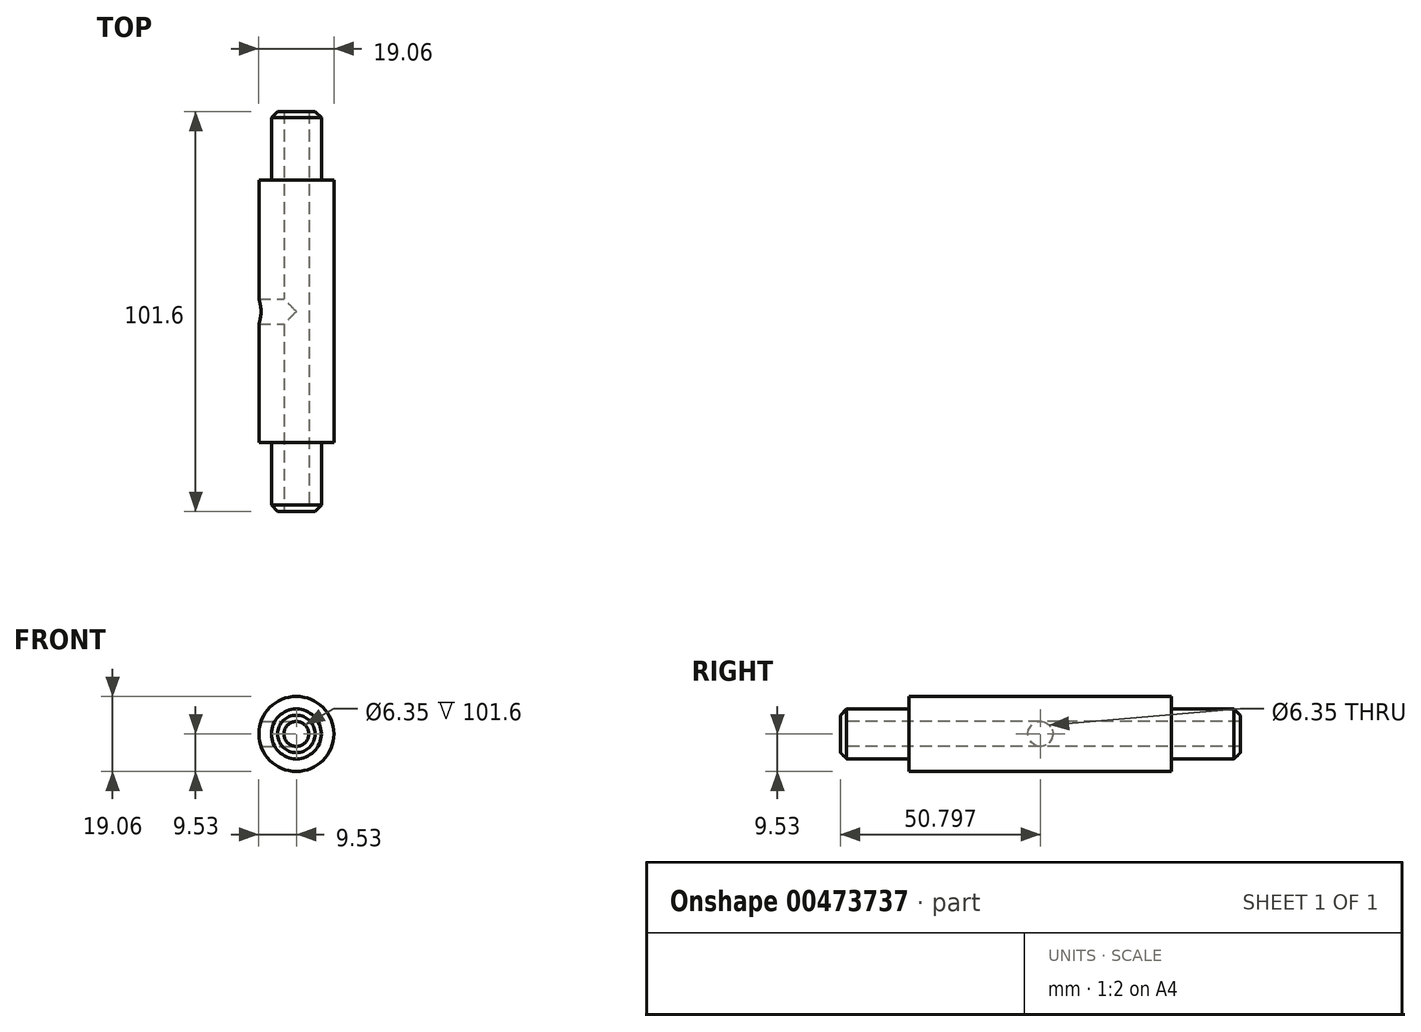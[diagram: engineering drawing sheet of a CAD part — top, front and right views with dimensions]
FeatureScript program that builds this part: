
annotation { "Feature Type Name" : "Feature", "Feature Type Description" : "" }
export const myFeature = defineFeature(function(context is Context, id is Id, definition is map)
    precondition{}
    {
        {
            var Q0;
            Q0=qCreatedBy(makeId("Right.planeOp"),FACE);
            var sketch = newSketch(context, id + "F0", { "sketchPlane" : qUnion([Q0])});
            skLineSegment(sketch, "E0", {"start": v(-10.14, 0) * mm, "end": v(91.46, 0) * mm});
            skLineSegment(sketch, "E1", {"start": v(-10.14, 3.18) * mm, "end": v(91.46, 3.18) * mm});
            skLineSegment(sketch, "E2", {"start": v(47, 3.17) * mm, "end": v(47, 0) * mm});
            skLineSegment(sketch, "E3", {"start": v(7.32, 3.17) * mm, "end": v(7.32, 9.53) * mm});
            skLineSegment(sketch, "E4", {"start": v(-10.14, 3.18) * mm, "end": v(-10.14, 6.35) * mm});
            skLineSegment(sketch, "E5", {"start": v(-10.14, 6.35) * mm, "end": v(7.32, 6.35) * mm});
            skPoint(sketch, "E5.endSnap0", {"position": v(7.32, 6.35) * mm});
            skLineSegment(sketch, "E6", {"start": v(7.32, 9.53) * mm, "end": v(74, 9.53) * mm});
            skLineSegment(sketch, "E7", {"start": v(91.46, 3.18) * mm, "end": v(91.46, 6.35) * mm});
            skLineSegment(sketch, "E8", {"start": v(74, 9.53) * mm, "end": v(74, 6.35) * mm});
            skLineSegment(sketch, "E9", {"start": v(74, 6.35) * mm, "end": v(91.46, 6.35) * mm});
            skSolve(sketch);
        }
        {
            var Q0;
            {var subQ0=sQuery(id+"F0.wireOp",EDGE,"E4");Q0=makeQuery(id+"F0.imprint","IMPRINT",FACE,{"disambiguationData":[TD([[makeQuery(id+"F0.imprint","IMPRINT",EDGE,{"derivedFrom":subQ0}),-1.0]])]});}
            var Q1;
            {var subQ0=sQuery(id+"F0.wireOp",EDGE,"E6");Q1=makeQuery(id+"F0.imprint","IMPRINT",FACE,{"disambiguationData":[TD([[makeQuery(id+"F0.imprint","IMPRINT",EDGE,{"derivedFrom":subQ0}),-1.0]])]});}
            var Q2;
            Q2=sQuery(id+"F0.wireOp",EDGE,"E0");
            revolve(context, id + "F1", {"entities" : qUnion([Q0, Q1]), "axis" : qUnion([Q2]), "revolveType" : RevolveType.FULL});
        }
        {
            var Q0;
            Q0=qCreatedBy(makeId("Right.planeOp"),FACE);
            var sketch = newSketch(context, id + "F2", { "sketchPlane" : qUnion([Q0])});
            skLineSegment(sketch, "E10.bottom", {"start": v(-30.78, -6.48) * mm, "end": v(-44.46, -6.48) * mm});
            skLineSegment(sketch, "E10.top", {"start": v(-30.78, 6.48) * mm, "end": v(-44.46, 6.48) * mm});
            skLineSegment(sketch, "E10.left", {"start": v(-30.78, -6.48) * mm, "end": v(-30.78, 6.48) * mm});
            skLineSegment(sketch, "E10.right", {"start": v(-44.46, -6.48) * mm, "end": v(-44.46, 6.48) * mm});
            skPoint(sketch, "E10.middle", {"position": v(-37.62, 0) * mm});
            skSolve(sketch);
        }
        {
            var Q0;
            Q0=makeQuery(id+"F2.imprint","IMPRINT",FACE,{"disambiguationData":[TD([[makeQuery(id+"F2.imprint","IMPRINT",EDGE,{"derivedFrom":sQuery(id+"F2.wireOp",EDGE,"E10.bottom")}),-1.0]])]});
            extrude(context, id + "F3", {"entities" : qUnion([Q0]), "depth" : 3 / 203.2 * mm});
        }
        {
            var Q0;
            Q0=makeQuery(id+"F3.opExtrude","CAP_FACE",FACE,{"disambiguationData":[OSD([sQuery(id+"F2.wireOp",EDGE,"E10.bottom"),sQuery(id+"F2.wireOp",EDGE,"E10.top"),sQuery(id+"F2.wireOp",EDGE,"E10.left"),sQuery(id+"F2.wireOp",EDGE,"E10.right")])],"isStart":false});
            var sketch = newSketch(context, id + "F4", { "sketchPlane" : qUnion([Q0])});
            skCircle(sketch, "E11", {"center": v(40.66, 0) * mm, "radius": 3.18 * mm});
            skSolve(sketch);
        }
        {
            var Q0;
            Q0=makeQuery(id+"F4.imprint","IMPRINT",FACE,{"disambiguationData":[TD([[makeQuery(id+"F4.imprint","IMPRINT",EDGE,{"derivedFrom":sQuery(id+"F4.wireOp",EDGE,"E11")}),1.0]])]});
            extrude(context, id + "F5", {"entities" : qUnion([Q0]), "operationType" : NewBodyOperationType.REMOVE, "oppositeDirection" : true, "depth" : 25.4 * mm});
        }
        {
            var Q0;
            Q0=makeQuery(id+"F1.opRevolve","SWEPT_EDGE",EDGE,{"disambiguationData":[OSD([sQuery(id+"F0.wireOp",EDGE,"E4"),sQuery(id+"F0.wireOp",EDGE,"E5")])]});
            var Q1;
            Q1=makeQuery(id+"F1.opRevolve","SWEPT_EDGE",EDGE,{"disambiguationData":[OSD([sQuery(id+"F0.wireOp",EDGE,"E7"),sQuery(id+"F0.wireOp",EDGE,"E9")])]});
            chamfer(context, id + "F6", {"entities" : qUnion([Q0, Q1]), "chamferType" : ChamferType.OFFSET_ANGLE, "width" : 1.59 * mm, "oppositeDirection" : false, "angle" : 45 * degree, "tangentPropagation" : true});
        }
        {
            var Q0;
            Q0=makeQuery(id+"F3.opExtrude","SWEPT_BODY",BODY,{"disambiguationData":[OSD([sQuery(id+"F2.wireOp",EDGE,"E10.bottom"),sQuery(id+"F2.wireOp",EDGE,"E10.top"),sQuery(id+"F2.wireOp",EDGE,"E10.left"),sQuery(id+"F2.wireOp",EDGE,"E10.right")])]});
            deleteBodies(context, id + "F7", {"entities" : qUnion([Q0])});
        }
    });
